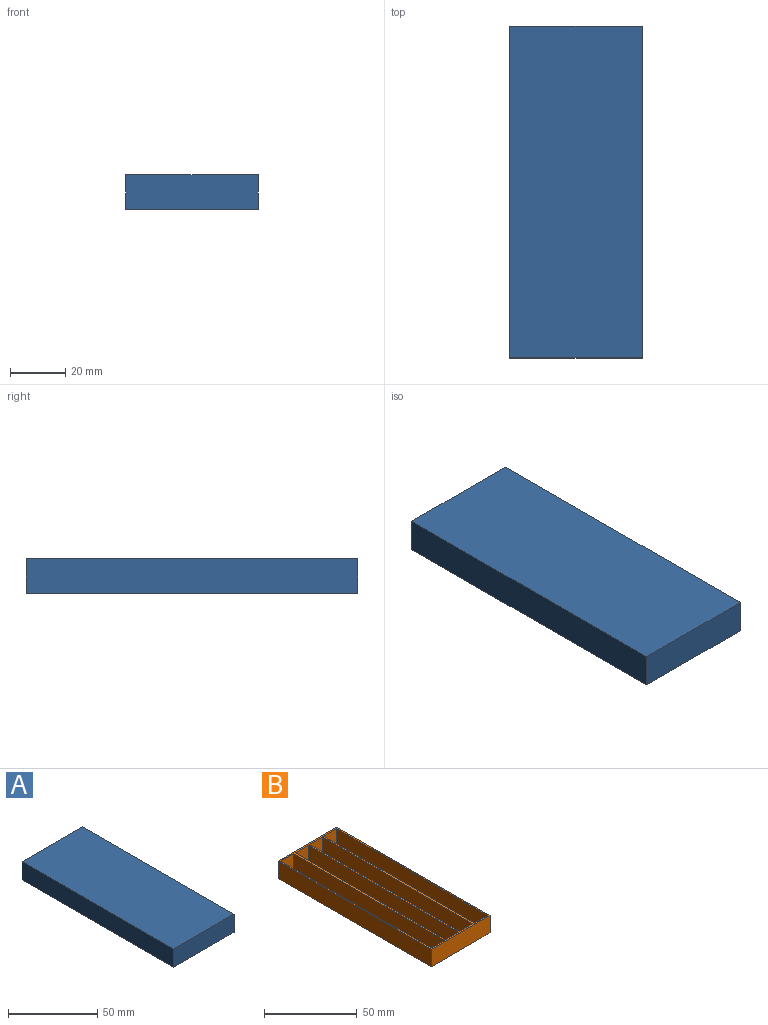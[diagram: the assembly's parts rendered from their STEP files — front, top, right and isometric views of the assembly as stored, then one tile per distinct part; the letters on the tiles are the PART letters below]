
ASSEMBLY  parts=2 mates=1
PART A: 11 faces, bbox 48x120x12.5 mm
  f0: plane 120x48mm, normal (0,0,-1), area 332mm2, adj f2,f3,f4,f5,f6,f7,f8,f9
  f1: plane 120x48mm, normal (0,0,1), area 5760mm2, adj f2,f3,f4,f5
  f2: plane 120x12.5mm, normal (-1,0,0), area 1500mm2, adj f0,f1,f4,f5
  f3: plane 120x12.5mm, normal (1,0,0), area 1500mm2, adj f0,f1,f4,f5
  f4: plane 48x12.5mm, normal (0,-1,0), area 600mm2, adj f0,f1,f2,f3
  f5: plane 48x12.5mm, normal (0,1,0), area 600mm2, adj f0,f1,f2,f3
  f6: plane 118x11.5mm, normal (1,0,0), area 1357mm2, adj f0,f7,f9,f10
  f7: plane 46x11.5mm, normal (0,-1,0), area 529mm2, adj f0,f6,f8,f10
  f8: plane 118x11.5mm, normal (-1,0,0), area 1357mm2, adj f0,f7,f9,f10
  f9: plane 46x11.5mm, normal (0,1,0), area 529mm2, adj f0,f6,f8,f10
  f10: plane 118x46mm, normal (0,0,-1), area 5428mm2, adj f6,f7,f8,f9
PART B: 26 faces, bbox 45x117x11.5 mm
  f0: plane 115x10mm, normal (-1,0,0), area 1150mm2, adj f1,f3,f18,f21
  f1: plane 115x10mm, normal (0,0,1), area 1150mm2, adj f0,f2,f18,f21
  f2: plane 115x10mm, normal (1,0,0), area 1150mm2, adj f1,f3,f18,f21
  f3: plane 117x45mm, normal (0,0,1), area 665mm2, adj f0,f2,f4,f6,f7,f9,f10,f12
  f4: plane 115x10mm, normal (-1,0,0), area 1150mm2, adj f3,f5,f17,f22
  f5: plane 115x10mm, normal (0,0,1), area 1150mm2, adj f4,f6,f17,f22
  f6: plane 115x10mm, normal (1,0,0), area 1150mm2, adj f3,f5,f17,f22
  f7: plane 115x10mm, normal (-1,0,0), area 1150mm2, adj f3,f8,f16,f23
  f8: plane 115x10mm, normal (0,0,1), area 1150mm2, adj f7,f9,f16,f23
  f9: plane 115x10mm, normal (1,0,0), area 1150mm2, adj f3,f8,f16,f23
  f10: plane 115x10mm, normal (-1,0,0), area 1150mm2, adj f3,f11,f19,f24
  f11: plane 115x10mm, normal (0,0,1), area 1150mm2, adj f10,f12,f19,f24
  f12: plane 115x10mm, normal (1,0,0), area 1150mm2, adj f3,f11,f19,f24
  f13: plane 117x11.5mm, normal (-1,0,0), area 1345.5mm2, adj f3,f14,f20,f25
  f14: plane 117x45mm, normal (0,0,-1), area 5265mm2, adj f13,f15,f20,f25
  f15: plane 117x11.5mm, normal (1,0,0), area 1345.5mm2, adj f3,f14,f20,f25
  f16: plane 10x10mm, normal (0,-1,0), area 100mm2, adj f3,f7,f8,f9
  f17: plane 10x10mm, normal (0,-1,0), area 100mm2, adj f3,f4,f5,f6
  f18: plane 10x10mm, normal (0,-1,0), area 100mm2, adj f0,f1,f2,f3
  f19: plane 10x10mm, normal (0,-1,0), area 100mm2, adj f3,f10,f11,f12
  f20: plane 45x11.5mm, normal (0,1,0), area 517.5mm2, adj f3,f13,f14,f15
  f21: plane 10x10mm, normal (0,1,0), area 100mm2, adj f0,f1,f2,f3
  f22: plane 10x10mm, normal (0,1,0), area 100mm2, adj f3,f4,f5,f6
  f23: plane 10x10mm, normal (0,1,0), area 100mm2, adj f3,f7,f8,f9
  f24: plane 10x10mm, normal (0,1,0), area 100mm2, adj f3,f10,f11,f12
  f25: plane 45x11.5mm, normal (0,-1,0), area 517.5mm2, adj f3,f13,f14,f15
PLACE A t=(0,0,-25.9)mm
PLACE B t=(18.09,-2.5,-27.84)mm
MATE slider B.f15 <-> A.f8  axis (1,0,0) through (40.11,-60,-27.45)mm
